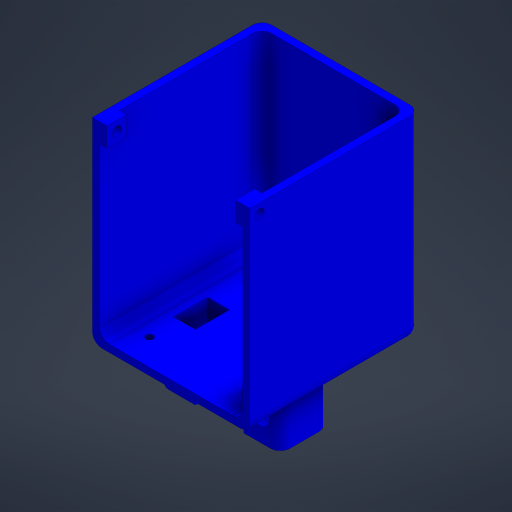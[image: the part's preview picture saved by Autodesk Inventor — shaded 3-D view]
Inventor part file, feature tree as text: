
AUTODESK INVENTOR PART (.ipt)
format: ipt  version: 2024 (Build 280153000, 153)  size: 346,624 bytes
history: native  units: mm
features: other x13, extrude x9, sketch x9, reference x6, fillet x3, mirror x1, projected_geometry x1
ambient origin geometry x8: Origin, YZ Plane, XZ Plane, XY Plane, X Axis, Y Axis, Z Axis, Center Point
bodies: Body1 (feature_tree)
feature tree (42):
  other  "Твердое тело1"
  extrude  "Выдавливание1"  Depth=4.0mm
  extrude  "Выдавливание2"  Depth=15.0mm
  fillet  "Сопряжение1"  Radius=20.0mm
  extrude  "Выдавливание3"  Depth=20.0mm
  extrude  "Выдавливание4"  Depth=4.0mm TaperAngle=0.0deg
  extrude  "Выдавливание5"  Depth=3.0mm
  extrude  "Выдавливание6"  Depth=3.0mm
  extrude  "Выдавливание7"  Depth=17.0mm TaperAngle=0.0deg
  extrude  "Выдавливание8"  Depth=4.0mm
  other  "РабПлоскость1"
  mirror  "Зеркальное отражение1"
  fillet  "Сопряжение3"  Radius=3.0mm
  fillet  "Сопряжение4"  [1 undecoded]
  extrude  "Выдавливание9"  Depth=65.0mm
  sketch  "Эскиз1"
  sketch  "Эскиз2"
  sketch  "Эскиз3"
  sketch  "Эскиз4"
  reference  "Ссылка1"
  reference  "Ссылка2"
  sketch  "Эскиз5"
  sketch  "Эскиз6"
  projected_geometry  "Спроецированная петля3"
  sketch  "Эскиз7"
  sketch  "Эскиз8"
  sketch  "Эскиз9"
  reference  "Ссылка3"
  reference  "Ссылка4"
  reference  "Ссылка5"
  reference  "Ссылка6"
  parser-record x2  (decoder bookkeeping rows leaked as tree rows — omitted from the tree; the rows remain in map.json)
  other  "main_assembly.iam"
  other  "back_box_asembly:1"
  other  "back_box:1"
  other  "tail_box_asembly.iam"
  other  "bts_asembly:1"
  other  "DIN 934 - заменено на DIN EN 24032/28673/28674 M3:3"
  other  "DIN 934 - заменено на DIN EN 24032/28673/28674 M3:1"
  other  "DIN 934 - заменено на DIN EN 24032/28673/28674 M3:2"
  other  "DIN 934 - заменено на DIN EN 24032/28673/28674 M3:4"
note: 1 required parameter value undecoded (feature->parameter linkage not recoverable at this tier; creation-order binding heuristic only, values carry confidence <= 0.55)
note: 2 file-system paths scrubbed to <path> (originals preserved in map.json)
